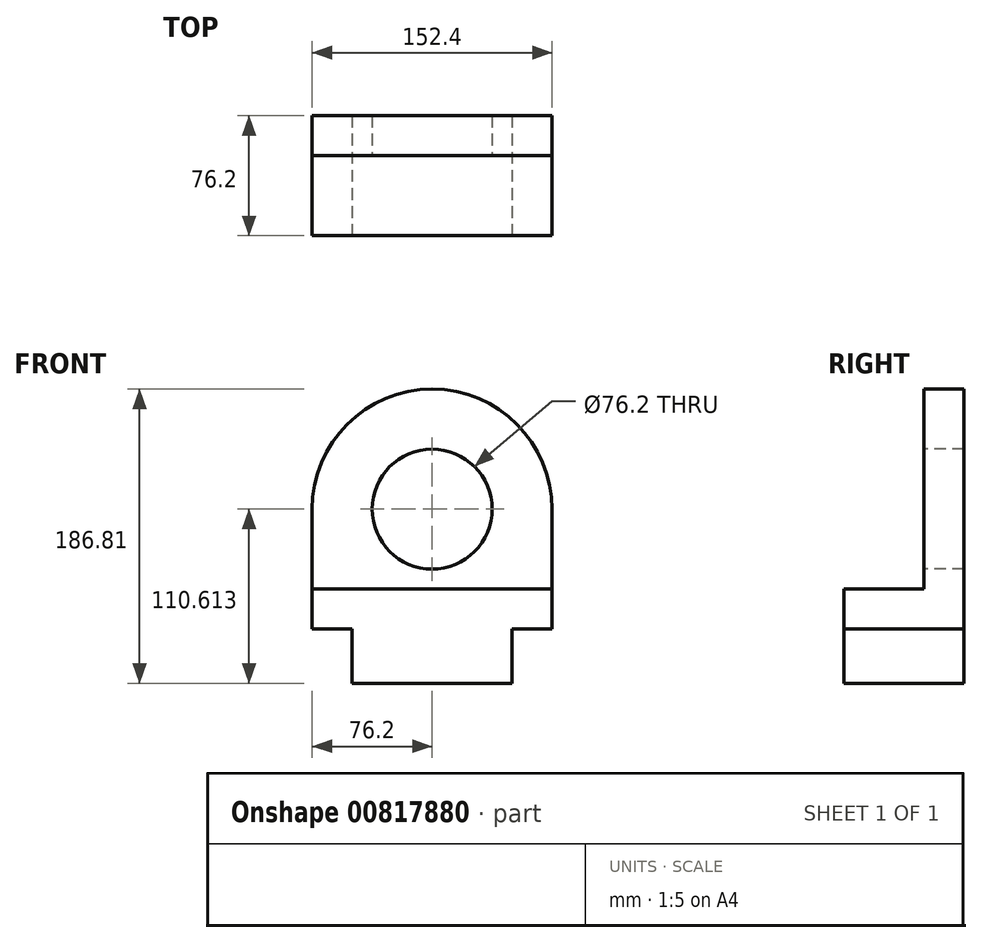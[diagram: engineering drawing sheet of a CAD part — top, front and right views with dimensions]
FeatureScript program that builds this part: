
annotation { "Feature Type Name" : "Feature", "Feature Type Description" : "" }
export const myFeature = defineFeature(function(context is Context, id is Id, definition is map)
    precondition{}
    {
        {
            var Q0;
            Q0=qCreatedBy(makeId("Front.planeOp"),FACE);
            var sketch = newSketch(context, id + "F0", { "sketchPlane" : qUnion([Q0])});
            skLineSegment(sketch, "E0", {"start": v(0, 0) * mm, "end": v(0, 34.41) * mm});
            skLineSegment(sketch, "E1", {"start": v(0, 34.41) * mm, "end": v(-25.4, 34.41) * mm});
            skLineSegment(sketch, "E2", {"start": v(0, 0) * mm, "end": v(101.6, 0) * mm});
            skLineSegment(sketch, "E3", {"start": v(101.6, 0) * mm, "end": v(101.6, 34.41) * mm});
            skLineSegment(sketch, "E4", {"start": v(101.6, 34.41) * mm, "end": v(127, 34.41) * mm});
            skLineSegment(sketch, "E5", {"start": v(127, 34.41) * mm, "end": v(127, 186.81) * mm});
            skLineSegment(sketch, "E6", {"start": v(-25.4, 34.41) * mm, "end": v(-25.4, 186.81) * mm});
            skLineSegment(sketch, "E7", {"start": v(-25.4, 186.81) * mm, "end": v(127, 186.81) * mm});
            skSolve(sketch);
        }
        {
            var Q0;
            Q0=makeQuery(id+"F0.imprint","IMPRINT",FACE,{"disambiguationData":[TD([[makeQuery(id+"F0.imprint","IMPRINT",EDGE,{"derivedFrom":sQuery(id+"F0.wireOp",EDGE,"E0")}),-1.0]])]});
            extrude(context, id + "F1", {"entities" : qUnion([Q0]), "oppositeDirection" : true, "depth" : 76.2 * mm, "offsetDistance" : 25.4 * mm});
        }
        {
            var Q0;
            Q0=makeQuery(id+"F1.opExtrude","SWEPT_FACE",FACE,{"disambiguationData":[OSD([sQuery(id+"F0.wireOp",EDGE,"E5")])]});
            var sketch = newSketch(context, id + "F2", { "sketchPlane" : qUnion([Q0])});
            skLineSegment(sketch, "E8.bottom", {"start": v(0, 186.81) * mm, "end": v(50.8, 186.81) * mm});
            skLineSegment(sketch, "E8.top", {"start": v(0, 59.81) * mm, "end": v(50.8, 59.81) * mm});
            skLineSegment(sketch, "E8.left", {"start": v(0, 186.81) * mm, "end": v(0, 59.81) * mm});
            skLineSegment(sketch, "E8.right", {"start": v(50.8, 186.81) * mm, "end": v(50.8, 59.81) * mm});
            skSolve(sketch);
        }
        {
            var Q0;
            Q0 = qSketchRegion(id + "F2", true);
            extrude(context, id + "F3", {"entities" : qUnion([Q0]), "operationType" : NewBodyOperationType.REMOVE, "endBound" : BoundingType.THROUGH_ALL, "oppositeDirection" : true, "depth" : 25.4 * mm, "offsetDistance" : 25.4 * mm});
        }
        {
            var Q0;
            Q0=makeQuery(id+"F3.boolean.opBoolean","COPY",FACE,{"derivedFrom":makeQuery(id+"F3.opExtrude","SWEPT_FACE",FACE,{"disambiguationData":[OSD([sQuery(id+"F2.wireOp",EDGE,"E8.right")])]})});
            var sketch = newSketch(context, id + "F4", { "sketchPlane" : qUnion([Q0])});
            skCircle(sketch, "E9", {"center": v(50.8, 110.61) * mm, "radius": 38.1 * mm});
            skSolve(sketch);
        }
        {
            var Q0;
            Q0 = qSketchRegion(id + "F4", true);
            extrude(context, id + "F5", {"entities" : qUnion([Q0]), "operationType" : NewBodyOperationType.REMOVE, "endBound" : BoundingType.THROUGH_ALL, "oppositeDirection" : true, "depth" : 25.4 * mm, "offsetDistance" : 25.4 * mm});
        }
        {
            var Q0;
            Q0=makeQuery(id+"F3.boolean.opBoolean","COPY",FACE,{"derivedFrom":makeQuery(id+"F3.opExtrude","SWEPT_FACE",FACE,{"disambiguationData":[OSD([sQuery(id+"F2.wireOp",EDGE,"E8.right")])]})});
            var sketch = newSketch(context, id + "F6", { "sketchPlane" : qUnion([Q0])});
            skLineSegment(sketch, "E10.top", {"start": v(-25.4, 186.81) * mm, "end": v(127, 186.81) * mm});
            skLineSegment(sketch, "E10.left", {"start": v(-25.4, 110.61) * mm, "end": v(-25.4, 186.81) * mm});
            skLineSegment(sketch, "E10.right", {"start": v(127, 110.61) * mm, "end": v(127, 186.81) * mm});
            skArc(sketch, "E11.trimOffspring", {"start": v(127, 110.61) * mm, "mid": v(50.8, 186.81) * mm, "end": v(-25.4, 110.61) * mm});
            skSolve(sketch);
        }
        {
            var Q0;
            {var subQ0=sQuery(id+"F6.wireOp",EDGE,"E10.left");Q0=makeQuery(id+"F6.imprint","IMPRINT",FACE,{"disambiguationData":[TD([[makeQuery(id+"F6.imprint","IMPRINT",EDGE,{"derivedFrom":subQ0}),1.0]])]});}
            var Q1;
            {var subQ0=sQuery(id+"F6.wireOp",EDGE,"E10.right");Q1=makeQuery(id+"F6.imprint","IMPRINT",FACE,{"disambiguationData":[TD([[makeQuery(id+"F6.imprint","IMPRINT",EDGE,{"derivedFrom":subQ0}),-1.0]])]});}
            extrude(context, id + "F7", {"entities" : qUnion([Q0, Q1]), "operationType" : NewBodyOperationType.REMOVE, "endBound" : BoundingType.THROUGH_ALL, "oppositeDirection" : true, "depth" : 25.4 * mm, "offsetDistance" : 25.4 * mm});
        }
    });
